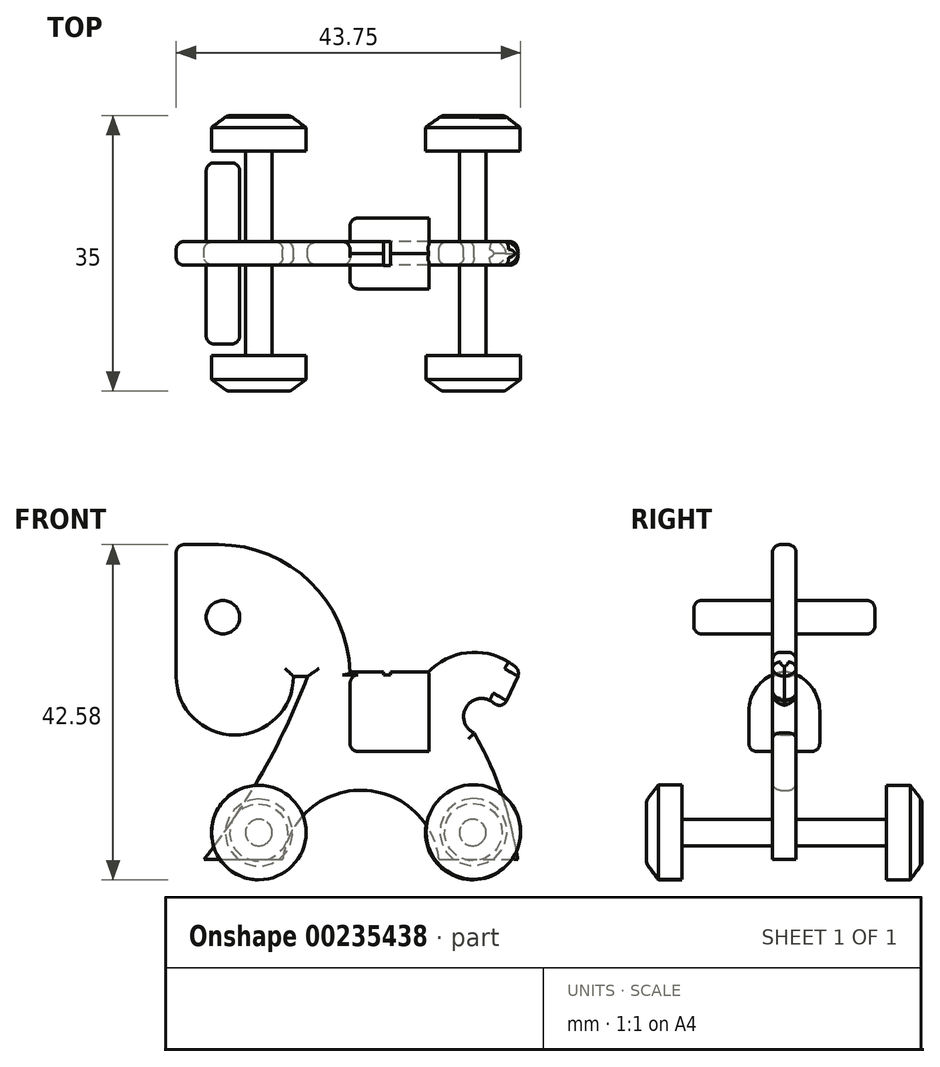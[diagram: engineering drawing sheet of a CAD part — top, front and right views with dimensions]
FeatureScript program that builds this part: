
annotation { "Feature Type Name" : "Feature", "Feature Type Description" : "" }
export const myFeature = defineFeature(function(context is Context, id is Id, definition is map)
    precondition{}
    {
        {
            var Q0;
            Q0=qCreatedBy(makeId("Front.planeOp"),FACE);
            var sketch = newSketch(context, id + "F0", { "sketchPlane" : qUnion([Q0])});
            skLineSegment(sketch, "E0", {"start": v(-55.34, 56.43) * mm, "end": v(-49.98, 56.43) * mm});
            skArc(sketch, "E1", {"start": v(-33.25, 40.31) * mm, "mid": v(-38.36, 51.75) * mm, "end": v(-49.98, 56.43) * mm});
            skLineSegment(sketch, "E2", {"start": v(-33.25, 40.31) * mm, "end": v(-23.25, 40.31) * mm});
            skArc(sketch, "E3", {"start": v(-11.59, 40.31) * mm, "mid": v(-17.42, 42.76) * mm, "end": v(-23.25, 40.31) * mm});
            skLineSegment(sketch, "E4", {"start": v(-55.34, 56.43) * mm, "end": v(-55.34, 39.7) * mm});
            skArc(sketch, "E5", {"start": v(-55.34, 39.7) * mm, "mid": v(-47.9, 32.24) * mm, "end": v(-40.44, 39.7) * mm});
            skLineSegment(sketch, "E6", {"start": v(-40.44, 39.7) * mm, "end": v(-38.64, 39.7) * mm});
            skArc(sketch, "E7", {"start": v(-51.8, 16.43) * mm, "mid": v(-44.34, 27.56) * mm, "end": v(-38.64, 39.7) * mm});
            skLineSegment(sketch, "E8", {"start": v(-51.8, 16.43) * mm, "end": v(-41.8, 16.43) * mm});
            skArc(sketch, "E9", {"start": v(-21.94, 16.43) * mm, "mid": v(-31.87, 25.23) * mm, "end": v(-41.8, 16.43) * mm});
            skArc(sketch, "E10", {"start": v(-14.24, 34.6) * mm, "mid": v(-17.77, 36.53) * mm, "end": v(-17.48, 32.51) * mm});
            skLineSegment(sketch, "E11", {"start": v(-14.24, 34.6) * mm, "end": v(-11.59, 40.31) * mm});
            skArc(sketch, "E12", {"start": v(-11.94, 16.43) * mm, "mid": v(-13.97, 24.73) * mm, "end": v(-17.48, 32.51) * mm});
            skLineSegment(sketch, "E13", {"start": v(-21.94, 16.43) * mm, "end": v(-11.94, 16.43) * mm});
            skCircle(sketch, "E14", {"center": v(-49.4, 47.21) * mm, "radius": 2.13 * mm});
            skCircle(sketch, "E15", {"center": v(-44.84, 19.85) * mm, "radius": 1.7 * mm});
            skCircle(sketch, "E16", {"center": v(-17.67, 19.85) * mm, "radius": 1.7 * mm});
            skSolve(sketch);
        }
        {
            var Q0;
            Q0 = qSketchRegion(id + "F0", true);
            extrude(context, id + "F1", {"entities" : qUnion([Q0]), "depth" : 3 * mm});
        }
        {
            var Q0;
            Q0=makeQuery(id+"F1.opExtrude","CAP_FACE",FACE,{"disambiguationData":[OSD([sQuery(id+"F0.wireOp",EDGE,"E0"),sQuery(id+"F0.wireOp",EDGE,"E1"),sQuery(id+"F0.wireOp",EDGE,"E2"),sQuery(id+"F0.wireOp",EDGE,"E3"),sQuery(id+"F0.wireOp",EDGE,"E4"),sQuery(id+"F0.wireOp",EDGE,"E5"),sQuery(id+"F0.wireOp",EDGE,"E6"),sQuery(id+"F0.wireOp",EDGE,"E7"),sQuery(id+"F0.wireOp",EDGE,"E8"),sQuery(id+"F0.wireOp",EDGE,"E9"),sQuery(id+"F0.wireOp",EDGE,"E10"),sQuery(id+"F0.wireOp",EDGE,"E11"),sQuery(id+"F0.wireOp",EDGE,"E12"),sQuery(id+"F0.wireOp",EDGE,"E13"),sQuery(id+"F0.wireOp",EDGE,"E14"),sQuery(id+"F0.wireOp",EDGE,"E15"),sQuery(id+"F0.wireOp",EDGE,"E16")])],"isStart":false});
            var sketch = newSketch(context, id + "F2", { "sketchPlane" : qUnion([Q0])});
            skSolve(sketch);
        }
        {
            var Q0;
            Q0=makeQuery(id+"F2.imprint","IMPRINT",FACE,{"disambiguationData":[TD([[makeQuery(id+"F2.imprint","IMPRINT",EDGE,{"derivedFrom":makeQuery(id+"F1.opExtrude","CAP_EDGE",EDGE,{"disambiguationData":[OSD([sQuery(id+"F0.wireOp",EDGE,"E15")])],"isStart":false})}),1.0]])]});
            var Q1;
            Q1=makeQuery(id+"F2.imprint","IMPRINT",FACE,{"disambiguationData":[TD([[makeQuery(id+"F2.imprint","IMPRINT",EDGE,{"derivedFrom":makeQuery(id+"F1.opExtrude","CAP_EDGE",EDGE,{"disambiguationData":[OSD([sQuery(id+"F0.wireOp",EDGE,"E16")])],"isStart":false})}),1.0]])]});
            extrude(context, id + "F3", {"entities" : qUnion([Q0, Q1]), "operationType" : NewBodyOperationType.ADD, "depth" : 13 * mm, "hasSecondDirection" : true, "secondDirectionOppositeDirection" : true, "secondDirectionDepth" : 16 * mm});
        }
        {
            var Q0;
            Q0=makeQuery(id+"F3.opExtrude","CAP_FACE",FACE,{"disambiguationData":[OSD([sQuery(id+"F0.wireOp",EDGE,"E15")])],"isStart":false});
            var sketch = newSketch(context, id + "F4", { "sketchPlane" : qUnion([Q0])});
            skCircle(sketch, "E17", {"center": v(-44.84, 19.85) * mm, "radius": 6 * mm});
            skCircle(sketch, "E18", {"center": v(-17.59, 19.94) * mm, "radius": 6 * mm});
            skSolve(sketch);
        }
        {
            var Q0;
            Q0=makeQuery(id+"F4.imprint","IMPRINT",FACE,{"disambiguationData":[TD([[makeQuery(id+"F4.imprint","IMPRINT",EDGE,{"derivedFrom":sQuery(id+"F4.wireOp",EDGE,"E18")}),1.0]])]});
            var Q1;
            Q1=makeQuery(id+"F4.imprint","IMPRINT",FACE,{"disambiguationData":[TD([[makeQuery(id+"F4.imprint","IMPRINT",EDGE,{"derivedFrom":sQuery(id+"F4.wireOp",EDGE,"E17")}),1.0]])]});
            var Q2;
            Q2=makeQuery(id+"F4.imprint","IMPRINT",FACE,{"disambiguationData":[TD([[makeQuery(id+"F4.imprint","IMPRINT",EDGE,{"derivedFrom":makeQuery(id+"F3.opExtrude","CAP_EDGE",EDGE,{"disambiguationData":[OSD([sQuery(id+"F0.wireOp",EDGE,"E15")])],"isStart":false})}),1.0]])]});
            extrude(context, id + "F5", {"entities" : qUnion([Q0, Q1, Q2]), "operationType" : NewBodyOperationType.ADD, "endBound" : BoundingType.SYMMETRIC, "oppositeDirection" : true, "depth" : 3 * mm});
        }
        {
            var Q0;
            Q0=makeQuery(id+"F3.opExtrude","CAP_FACE",FACE,{"disambiguationData":[OSD([sQuery(id+"F0.wireOp",EDGE,"E16")])],"isStart":true});
            var sketch = newSketch(context, id + "F6", { "sketchPlane" : qUnion([Q0])});
            skCircle(sketch, "E19", {"center": v(44.85, 19.85) * mm, "radius": 6 * mm});
            skCircle(sketch, "E20", {"center": v(17.67, 19.85) * mm, "radius": 6 * mm});
            skCircle(sketch, "E21", {"center": v(44.85, 19.85) * mm, "radius": 6.02 * mm});
            skSolve(sketch);
        }
        {
            var Q0;
            Q0=makeQuery(id+"F6.imprint","IMPRINT",FACE,{"disambiguationData":[TD([[makeQuery(id+"F6.imprint","IMPRINT",EDGE,{"derivedFrom":sQuery(id+"F6.wireOp",EDGE,"E20")}),1.0]])]});
            var Q1;
            Q1=makeQuery(id+"F6.imprint","IMPRINT",FACE,{"disambiguationData":[TD([[makeQuery(id+"F6.imprint","IMPRINT",EDGE,{"derivedFrom":sQuery(id+"F6.wireOp",EDGE,"E19")}),1.0]])]});
            var Q2;
            Q2=makeQuery(id+"F6.imprint","IMPRINT",FACE,{"disambiguationData":[TD([[makeQuery(id+"F6.imprint","IMPRINT",EDGE,{"derivedFrom":makeQuery(id+"F3.opExtrude","CAP_EDGE",EDGE,{"disambiguationData":[OSD([sQuery(id+"F0.wireOp",EDGE,"E16")])],"isStart":true})}),-1.0]])]});
            extrude(context, id + "F7", {"entities" : qUnion([Q0, Q1, Q2]), "operationType" : NewBodyOperationType.ADD, "endBound" : BoundingType.SYMMETRIC, "oppositeDirection" : true, "depth" : 3 * mm});
        }
        {
            var Q0;
            Q0=makeQuery(id+"F1.opExtrude","CAP_FACE",FACE,{"disambiguationData":[OSD([sQuery(id+"F0.wireOp",EDGE,"E0"),sQuery(id+"F0.wireOp",EDGE,"E1"),sQuery(id+"F0.wireOp",EDGE,"E2"),sQuery(id+"F0.wireOp",EDGE,"E3"),sQuery(id+"F0.wireOp",EDGE,"E4"),sQuery(id+"F0.wireOp",EDGE,"E5"),sQuery(id+"F0.wireOp",EDGE,"E6"),sQuery(id+"F0.wireOp",EDGE,"E7"),sQuery(id+"F0.wireOp",EDGE,"E8"),sQuery(id+"F0.wireOp",EDGE,"E9"),sQuery(id+"F0.wireOp",EDGE,"E10"),sQuery(id+"F0.wireOp",EDGE,"E11"),sQuery(id+"F0.wireOp",EDGE,"E12"),sQuery(id+"F0.wireOp",EDGE,"E13"),sQuery(id+"F0.wireOp",EDGE,"E14"),sQuery(id+"F0.wireOp",EDGE,"E15"),sQuery(id+"F0.wireOp",EDGE,"E16")])],"isStart":true});
            var sketch = newSketch(context, id + "F8", { "sketchPlane" : qUnion([Q0])});
            skLineSegment(sketch, "E22", {"start": v(23.25, 40.31) * mm, "end": v(23.25, 30.15) * mm});
            skLineSegment(sketch, "E23", {"start": v(23.25, 30.15) * mm, "end": v(33.25, 30.15) * mm});
            skLineSegment(sketch, "E24", {"start": v(33.25, 30.15) * mm, "end": v(33.25, 40.31) * mm});
            skLineSegment(sketch, "E25", {"start": v(33.25, 40.31) * mm, "end": v(23.25, 40.31) * mm});
            skSolve(sketch);
        }
        {
            var Q0;
            Q0=makeQuery(id+"F8.imprint","IMPRINT",FACE,{"disambiguationData":[TD([[makeQuery(id+"F8.imprint","IMPRINT",EDGE,{"derivedFrom":sQuery(id+"F8.wireOp",EDGE,"E22")}),1.0]])]});
            extrude(context, id + "F9", {"entities" : qUnion([Q0]), "operationType" : NewBodyOperationType.ADD, "depth" : 3 * mm, "hasSecondDirection" : true, "secondDirectionOppositeDirection" : true, "secondDirectionDepth" : 6 * mm});
        }
        {
            var Q0;
            Q0=makeQuery(id+"F9.opExtrude","CAP_EDGE",EDGE,{"disambiguationData":[OSD([sQuery(id+"F8.wireOp",EDGE,"E25")])],"isStart":false});
            var Q1;
            Q1=makeQuery(id+"F9.opExtrude","CAP_EDGE",EDGE,{"disambiguationData":[OSD([sQuery(id+"F8.wireOp",EDGE,"E25")])],"isStart":true});
            fillet(context, id + "F10", {"entities" : qUnion([Q0, Q1]), "radius" : 5 * mm, "tangentPropagation" : true, "allowEdgeOverflow" : false});
        }
        {
            var Q0;
            Q0=makeQuery(id+"F8.imprint","IMPRINT",FACE,{"disambiguationData":[TD([[makeQuery(id+"F8.imprint","IMPRINT",EDGE,{"derivedFrom":makeQuery(id+"F1.opExtrude","CAP_EDGE",EDGE,{"disambiguationData":[OSD([sQuery(id+"F0.wireOp",EDGE,"E14")])],"isStart":true})}),-1.0]])]});
            extrude(context, id + "F11", {"entities" : qUnion([Q0]), "operationType" : NewBodyOperationType.ADD, "depth" : 10 * mm, "hasSecondDirection" : true, "secondDirectionOppositeDirection" : true, "secondDirectionDepth" : 13 * mm});
        }
        {
            var Q0;
            Q0=makeQuery(id+"F4.imprint","IMPRINT",FACE,{"disambiguationData":[TD([[makeQuery(id+"F4.imprint","IMPRINT",EDGE,{"derivedFrom":sQuery(id+"F4.wireOp",EDGE,"E17")}),1.0]])]});
            var Q1;
            Q1=makeQuery(id+"F4.imprint","IMPRINT",FACE,{"disambiguationData":[TD([[makeQuery(id+"F4.imprint","IMPRINT",EDGE,{"derivedFrom":sQuery(id+"F4.wireOp",EDGE,"E18")}),1.0]])]});
            cPlane(context, id + "F12", {"entities" : qUnion([Q0, Q1]), "cplaneType" : CPlaneType.MID_PLANE, "offset" : 25 * mm, "width" : 150 * mm, "height" : 150 * mm});
        }
        {
            var Q0;
            Q0=qCreatedBy(id+"F12.planeOp",FACE);
            cPlane(context, id + "F13", {"entities" : qUnion([Q0]), "cplaneType" : CPlaneType.OFFSET, "offset" : 3 * mm, "width" : 150 * mm, "height" : 150 * mm});
        }
        {
            var Q0;
            Q0=qCreatedBy(id+"F13.planeOp",FACE);
            var sketch = newSketch(context, id + "F14", { "sketchPlane" : qUnion([Q0])});
            skCircle(sketch, "E26", {"center": v(-44.84, 19.85) * mm, "radius": 4 * mm});
            skCircle(sketch, "E27", {"center": v(-17.59, 19.94) * mm, "radius": 4 * mm});
            skSolve(sketch);
        }
        {
            var Q1;
            Q1=makeQuery(id+"F5.opExtrude","CAP_FACE",FACE,{"disambiguationData":[OSD([sQuery(id+"F4.wireOp",EDGE,"E17")])],"isStart":true});
            var Q2;
            Q2=makeQuery(id+"F14.imprint","IMPRINT",FACE,{"disambiguationData":[TD([[makeQuery(id+"F14.imprint","IMPRINT",EDGE,{"derivedFrom":sQuery(id+"F14.wireOp",EDGE,"E26")}),1.0]])]});
            loft(context, id + "F15", {"operationType" : NewBodyOperationType.ADD, "sheetProfilesArray" : [{ "sheetProfileEntities" : qUnion([Q1]) }, { "sheetProfileEntities" : qUnion([Q2]) }]});
        }
        {
            var Q0;
            Q0=qCreatedBy(id+"F13.planeOp",FACE);
            var sketch = newSketch(context, id + "F16", { "sketchPlane" : qUnion([Q0])});
            skCircle(sketch, "E28", {"center": v(-17.59, 19.94) * mm, "radius": 4 * mm});
            skSolve(sketch);
        }
        {
            var Q1;
            Q1=makeQuery(id+"F5.opExtrude","CAP_FACE",FACE,{"disambiguationData":[OSD([sQuery(id+"F4.wireOp",EDGE,"E18")])],"isStart":true});
            var Q2;
            Q2=makeQuery(id+"F16.imprint","IMPRINT",FACE,{"disambiguationData":[TD([[makeQuery(id+"F16.imprint","IMPRINT",EDGE,{"derivedFrom":sQuery(id+"F16.wireOp",EDGE,"E28")}),1.0]])]});
            loft(context, id + "F17", {"operationType" : NewBodyOperationType.ADD, "sheetProfilesArray" : [{ "sheetProfileEntities" : qUnion([Q1]) }, { "sheetProfileEntities" : qUnion([Q2]) }]});
        }
        {
            var Q0;
            Q0=makeQuery(id+"F7.opExtrude","CAP_FACE",FACE,{"disambiguationData":[OSD([sQuery(id+"F6.wireOp",EDGE,"E20")])],"isStart":true});
            var sketch = newSketch(context, id + "F18", { "sketchPlane" : qUnion([Q0])});
            skSolve(sketch);
        }
        {
            var Q0;
            Q0=makeQuery(id+"F18.imprint","IMPRINT",FACE,{"disambiguationData":[TD([[makeQuery(id+"F18.imprint","IMPRINT",EDGE,{"derivedFrom":makeQuery(id+"F7.opExtrude","CAP_EDGE",EDGE,{"disambiguationData":[OSD([sQuery(id+"F6.wireOp",EDGE,"E20")])],"isStart":true})}),1.0]])]});
            var Q1;
            Q1=makeQuery(id+"F7.opExtrude","CAP_FACE",FACE,{"disambiguationData":[OSD([sQuery(id+"F6.wireOp",EDGE,"E19")])],"isStart":true});
            cPlane(context, id + "F19", {"entities" : qUnion([Q0, Q1]), "cplaneType" : CPlaneType.MID_PLANE, "offset" : 25 * mm, "width" : 150 * mm, "height" : 150 * mm});
        }
        {
            var Q0;
            Q0=qCreatedBy(id+"F19.planeOp",FACE);
            cPlane(context, id + "F20", {"entities" : qUnion([Q0]), "cplaneType" : CPlaneType.OFFSET, "offset" : 1.5 * mm, "width" : 150 * mm, "height" : 150 * mm});
        }
        {
            var Q0;
            Q0=qCreatedBy(id+"F20.planeOp",FACE);
            var sketch = newSketch(context, id + "F21", { "sketchPlane" : qUnion([Q0])});
            skCircle(sketch, "E29", {"center": v(44.84, 19.85) * mm, "radius": 4 * mm});
            skSolve(sketch);
        }
        {
            var Q0;
            Q0=makeQuery(id+"F7.opExtrude","CAP_FACE",FACE,{"disambiguationData":[OSD([sQuery(id+"F6.wireOp",EDGE,"E19")])],"isStart":true});
            var Q1;
            Q1=makeQuery(id+"F21.imprint","IMPRINT",FACE,{"disambiguationData":[TD([[makeQuery(id+"F21.imprint","IMPRINT",EDGE,{"derivedFrom":sQuery(id+"F21.wireOp",EDGE,"E29")}),1.0]])]});
            loft(context, id + "F22", {"sheetProfilesArray" : [{ "sheetProfileEntities" : qUnion([Q0]) }, { "sheetProfileEntities" : qUnion([Q1]) }]});
        }
        {
            var Q0;
            Q0=qCreatedBy(id+"F20.planeOp",FACE);
            var sketch = newSketch(context, id + "F23", { "sketchPlane" : qUnion([Q0])});
            skCircle(sketch, "E30", {"center": v(17.59, 19.94) * mm, "radius": 4 * mm});
            skSolve(sketch);
        }
        {
            var Q0;
            Q0=makeQuery(id+"F18.imprint","IMPRINT",FACE,{"disambiguationData":[TD([[makeQuery(id+"F18.imprint","IMPRINT",EDGE,{"derivedFrom":makeQuery(id+"F7.opExtrude","CAP_EDGE",EDGE,{"disambiguationData":[OSD([sQuery(id+"F6.wireOp",EDGE,"E20")])],"isStart":true})}),1.0]])]});
            var Q1;
            Q1=makeQuery(id+"F23.imprint","IMPRINT",FACE,{"disambiguationData":[TD([[makeQuery(id+"F23.imprint","IMPRINT",EDGE,{"derivedFrom":sQuery(id+"F23.wireOp",EDGE,"E30")}),1.0]])]});
            loft(context, id + "F24", {"sheetProfilesArray" : [{ "sheetProfileEntities" : qUnion([Q0]) }, { "sheetProfileEntities" : qUnion([Q1]) }]});
        }
        {
            var Q0;
            Q0=makeQuery(id+"F1.opExtrude","CAP_EDGE",EDGE,{"disambiguationData":[OSD([sQuery(id+"F0.wireOp",EDGE,"E0")])],"isStart":false});
            var Q1;
            Q1=makeQuery(id+"F1.opExtrude","CAP_EDGE",EDGE,{"disambiguationData":[OSD([sQuery(id+"F0.wireOp",EDGE,"E1")])],"isStart":true});
            fillet(context, id + "F25", {"entities" : qUnion([Q0, Q1]), "radius" : 1 * mm, "tangentPropagation" : true, "allowEdgeOverflow" : false});
        }
        {
            var Q0;
            Q0=makeQuery(id+"F1.opExtrude","CAP_EDGE",EDGE,{"disambiguationData":[OSD([sQuery(id+"F0.wireOp",EDGE,"E11")])],"isStart":true});
            var Q1;
            Q1=makeQuery(id+"F1.opExtrude","CAP_EDGE",EDGE,{"disambiguationData":[OSD([sQuery(id+"F0.wireOp",EDGE,"E11")])],"isStart":false});
            fillet(context, id + "F26", {"entities" : qUnion([Q0, Q1]), "radius" : 2 * mm, "tangentPropagation" : true, "allowEdgeOverflow" : false});
        }
        {
            var Q0;
            Q0=makeQuery(id+"F11.opExtrude","CAP_EDGE",EDGE,{"disambiguationData":[OSD([sQuery(id+"F0.wireOp",EDGE,"E14")])],"isStart":false});
            var Q1;
            Q1=makeQuery(id+"F11.opExtrude","CAP_EDGE",EDGE,{"disambiguationData":[OSD([sQuery(id+"F0.wireOp",EDGE,"E14")])],"isStart":true});
            var Q2;
            Q2=makeQuery(id+"F1.opExtrude","CAP_EDGE",EDGE,{"disambiguationData":[OSD([sQuery(id+"F0.wireOp",EDGE,"E3")])],"isStart":true});
            var Q3;
            Q3=makeQuery(id+"F1.opExtrude","CAP_EDGE",EDGE,{"disambiguationData":[OSD([sQuery(id+"F0.wireOp",EDGE,"E3")])],"isStart":false});
            fillet(context, id + "F27", {"entities" : qUnion([Q0, Q1, Q2, Q3]), "radius" : 1 * mm, "tangentPropagation" : true, "allowEdgeOverflow" : false});
        }
        {
            var Q0;
            Q0=makeQuery(id+"F9.opExtrude","CAP_EDGE",EDGE,{"disambiguationData":[OSD([sQuery(id+"F8.wireOp",EDGE,"E23")])],"isStart":true});
            var Q1;
            Q1=makeQuery(id+"F9.opExtrude","CAP_EDGE",EDGE,{"disambiguationData":[OSD([sQuery(id+"F8.wireOp",EDGE,"E23")])],"isStart":false});
            fillet(context, id + "F28", {"entities" : qUnion([Q0, Q1]), "radius" : 1 * mm, "tangentPropagation" : true, "allowEdgeOverflow" : false});
        }
        {
            var Q0;
            Q0=makeQuery(id+"F15.opLoft","MID_CAP_EDGE",EDGE,{"disambiguationData":[OSD([sQuery(id+"F4.wireOp",EDGE,"E17"),sQuery(id+"F14.wireOp",EDGE,"E26")])],"capPos":1.0});
            var Q1;
            Q1=makeQuery(id+"F17.opLoft","MID_CAP_EDGE",EDGE,{"disambiguationData":[OSD([sQuery(id+"F4.wireOp",EDGE,"E18"),sQuery(id+"F16.wireOp",EDGE,"E28")])],"capPos":1.0});
            var Q2;
            Q2=makeQuery(id+"F24.opLoft","MID_CAP_EDGE",EDGE,{"disambiguationData":[OSD([sQuery(id+"F6.wireOp",EDGE,"E20"),sQuery(id+"F23.wireOp",EDGE,"E30")])],"capPos":1.0});
            var Q3;
            Q3=makeQuery(id+"F22.opLoft","MID_CAP_EDGE",EDGE,{"disambiguationData":[OSD([sQuery(id+"F6.wireOp",EDGE,"E19"),sQuery(id+"F21.wireOp",EDGE,"E29")])],"capPos":1.0});
            var Q4;
            Q4=makeQuery(id+"F1.opExtrude","CAP_EDGE",EDGE,{"disambiguationData":[OSD([sQuery(id+"F0.wireOp",EDGE,"E4")])],"isStart":true});
            var Q5;
            Q5=makeQuery(id+"F1.opExtrude","CAP_EDGE",EDGE,{"disambiguationData":[OSD([sQuery(id+"F0.wireOp",EDGE,"E10")])],"isStart":true});
            var Q6;
            Q6=makeQuery(id+"F1.opExtrude","CAP_EDGE",EDGE,{"disambiguationData":[OSD([sQuery(id+"F0.wireOp",EDGE,"E10")])],"isStart":false});
            var Q7;
            Q7=makeQuery(id+"F1.opExtrude","CAP_EDGE",EDGE,{"disambiguationData":[OSD([sQuery(id+"F0.wireOp",EDGE,"E12")])],"isStart":false});
            var Q8;
            Q8=makeQuery(id+"F1.opExtrude","CAP_EDGE",EDGE,{"disambiguationData":[OSD([sQuery(id+"F0.wireOp",EDGE,"E12")])],"isStart":true});
            fillet(context, id + "F29", {"entities" : qUnion([Q0, Q1, Q2, Q3, Q4, Q5, Q6, Q7, Q8]), "radius" : 1 * mm, "tangentPropagation" : true, "allowEdgeOverflow" : false});
        }
        {
            var Q0;
            Q0=makeQuery(id+"F1.opExtrude","CAP_EDGE",EDGE,{"disambiguationData":[OSD([sQuery(id+"F0.wireOp",EDGE,"E6")])],"isStart":false});
            var Q1;
            Q1=makeQuery(id+"F1.opExtrude","CAP_EDGE",EDGE,{"disambiguationData":[OSD([sQuery(id+"F0.wireOp",EDGE,"E7")])],"isStart":false});
            var Q2;
            Q2=makeQuery(id+"F1.opExtrude","CAP_EDGE",EDGE,{"disambiguationData":[OSD([sQuery(id+"F0.wireOp",EDGE,"E6")])],"isStart":true});
            var Q3;
            Q3=makeQuery(id+"F1.opExtrude","CAP_EDGE",EDGE,{"disambiguationData":[OSD([sQuery(id+"F0.wireOp",EDGE,"E7")])],"isStart":true});
            var Q4;
            Q4=makeQuery(id+"F1.opExtrude","CAP_EDGE",EDGE,{"disambiguationData":[OSD([sQuery(id+"F0.wireOp",EDGE,"E9")])],"isStart":false});
            var Q5;
            Q5=makeQuery(id+"F1.opExtrude","CAP_EDGE",EDGE,{"disambiguationData":[OSD([sQuery(id+"F0.wireOp",EDGE,"E9")])],"isStart":true});
            fillet(context, id + "F30", {"entities" : qUnion([Q0, Q1, Q2, Q3, Q4, Q5]), "radius" : 1 * mm, "tangentPropagation" : true, "allowEdgeOverflow" : false});
        }
        {
            var Q0;
            {var subQ1=sQuery(id+"F8.wireOp",EDGE,"E25");var subQ2=sQuery(id+"F8.wireOp",EDGE,"E24");var subQ3=sQuery(id+"F8.wireOp",EDGE,"E23");Q0=makeQuery(id+"F10.opFillet","BLEND_EDGE",EDGE,{"blendedFrom":[makeQuery(id+"F9.opExtrude","CAP_EDGE",EDGE,{"disambiguationData":[OSD([subQ1])],"isStart":false}),makeQuery(id+"F9.boolean.opBoolean","SPLIT",FACE,{"disambiguationData":[TD([makeQuery(id+"F9.opExtrude","CAP_FACE",FACE,{"disambiguationData":[OSD([sQuery(id+"F8.wireOp",EDGE,"E22"),subQ3,subQ2,subQ1])],"isStart":false})])],"derivedFrom":makeQuery(id+"F9.opExtrude","SWEPT_FACE",FACE,{"disambiguationData":[OSD([subQ2])]})})],"blendedInto":[makeQuery(id+"F9.boolean.opBoolean","SPLIT",FACE,{"disambiguationData":[TD([makeQuery(id+"F9.opExtrude","CAP_FACE",FACE,{"disambiguationData":[OSD([sQuery(id+"F8.wireOp",EDGE,"E22"),subQ3,subQ2,subQ1])],"isStart":false})])],"derivedFrom":makeQuery(id+"F9.opExtrude","SWEPT_FACE",FACE,{"disambiguationData":[OSD([subQ2])]})})]});}
            var Q1;
            {var subQ1=sQuery(id+"F8.wireOp",EDGE,"E25");var subQ2=sQuery(id+"F8.wireOp",EDGE,"E24");var subQ3=sQuery(id+"F8.wireOp",EDGE,"E23");Q1=makeQuery(id+"F10.opFillet","BLEND_EDGE",EDGE,{"blendedFrom":[makeQuery(id+"F9.opExtrude","CAP_EDGE",EDGE,{"disambiguationData":[OSD([subQ1])],"isStart":true}),makeQuery(id+"F9.boolean.opBoolean","SPLIT",FACE,{"disambiguationData":[TD([makeQuery(id+"F9.opExtrude","CAP_FACE",FACE,{"disambiguationData":[OSD([sQuery(id+"F8.wireOp",EDGE,"E22"),subQ3,subQ2,subQ1])],"isStart":true})])],"derivedFrom":makeQuery(id+"F9.opExtrude","SWEPT_FACE",FACE,{"disambiguationData":[OSD([subQ2])]})})],"blendedInto":[makeQuery(id+"F9.boolean.opBoolean","SPLIT",FACE,{"disambiguationData":[TD([makeQuery(id+"F9.opExtrude","CAP_FACE",FACE,{"disambiguationData":[OSD([sQuery(id+"F8.wireOp",EDGE,"E22"),subQ3,subQ2,subQ1])],"isStart":true})])],"derivedFrom":makeQuery(id+"F9.opExtrude","SWEPT_FACE",FACE,{"disambiguationData":[OSD([subQ2])]})})]});}
            fillet(context, id + "F31", {"entities" : qUnion([Q0, Q1]), "radius" : 1 * mm, "tangentPropagation" : true, "allowEdgeOverflow" : false});
        }
        {
            var Q0;
            Q0=qCreatedBy(makeId("Front.planeOp"),FACE);
            var sketch = newSketch(context, id + "F32", { "sketchPlane" : qUnion([Q0])});
            skLineSegment(sketch, "E31.bottom", {"start": v(-29, 40.8) * mm, "end": v(-28.11, 40.8) * mm});
            skLineSegment(sketch, "E31.top", {"start": v(-29, 39.89) * mm, "end": v(-28.11, 39.89) * mm});
            skLineSegment(sketch, "E31.left", {"start": v(-29, 40.8) * mm, "end": v(-29, 39.89) * mm});
            skLineSegment(sketch, "E31.right", {"start": v(-28.11, 40.8) * mm, "end": v(-28.11, 39.89) * mm});
            skSolve(sketch);
        }
        {
            var Q0;
            Q0=makeQuery(id+"F32.imprint","IMPRINT",FACE,{"disambiguationData":[TD([[makeQuery(id+"F32.imprint","IMPRINT",EDGE,{"derivedFrom":sQuery(id+"F32.wireOp",EDGE,"E31.bottom")}),-1.0]])]});
            extrude(context, id + "F33", {"entities" : qUnion([Q0]), "operationType" : NewBodyOperationType.REMOVE, "depth" : 25 * mm, "hasSecondDirection" : true, "secondDirectionOppositeDirection" : true, "secondDirectionDepth" : 25 * mm});
        }
    });
